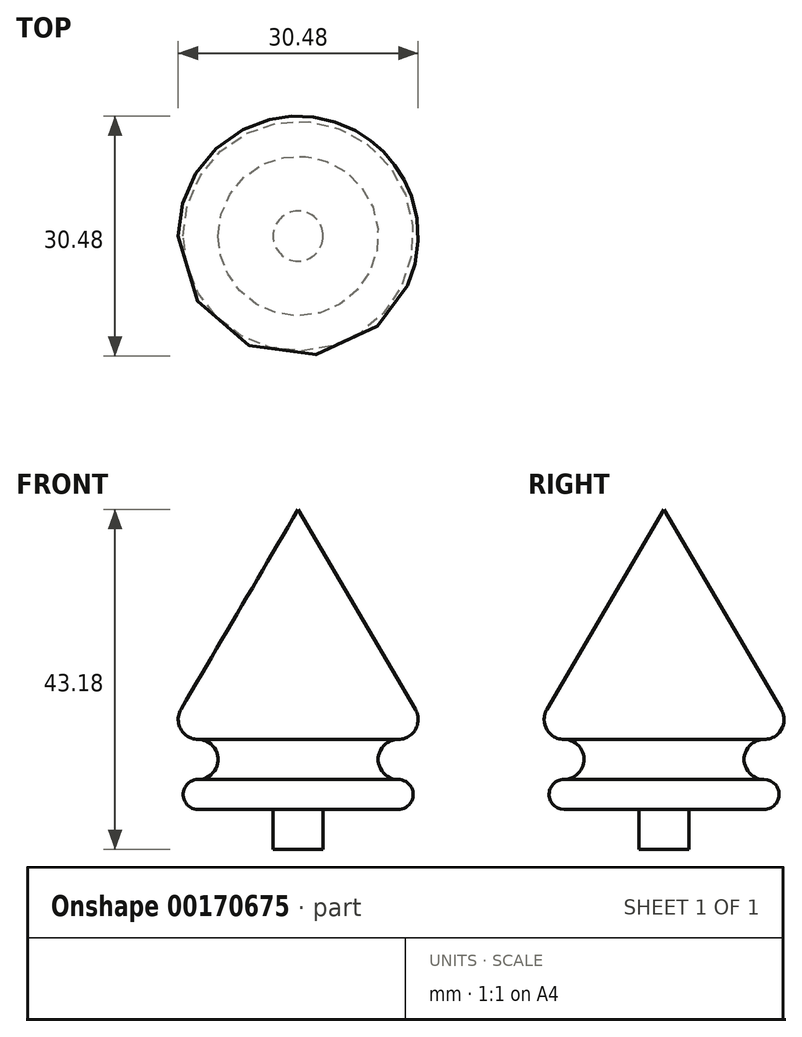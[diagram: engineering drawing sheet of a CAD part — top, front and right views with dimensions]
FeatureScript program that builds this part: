
annotation { "Feature Type Name" : "Feature", "Feature Type Description" : "" }
export const myFeature = defineFeature(function(context is Context, id is Id, definition is map)
    precondition{}
    {
        {
            var Q0;
            Q0=qCreatedBy(makeId("Front.planeOp"),FACE);
            var sketch = newSketch(context, id + "F0", { "sketchPlane" : qUnion([Q0])});
            skLineSegment(sketch, "E0", {"start": v(0, -5.08) * mm, "end": v(0, 38.1) * mm});
            skLineSegment(sketch, "E1", {"start": v(0, 38.1) * mm, "end": v(-14.9, 12.72) * mm});
            skLineSegment(sketch, "E2", {"start": v(0, -5.08) * mm, "end": v(-3.18, -5.08) * mm});
            skLineSegment(sketch, "E3", {"start": v(-3.18, -5.08) * mm, "end": v(-3.18, 0) * mm});
            skLineSegment(sketch, "E4", {"start": v(-3.18, 0) * mm, "end": v(-12.7, 0) * mm});
            skArc(sketch, "E5", {"start": v(-12.7, 3.81) * mm, "mid": v(-14.6, 1.9) * mm, "end": v(-12.7, 0) * mm});
            skArc(sketch, "E6", {"start": v(-12.7, 3.81) * mm, "mid": v(-10.16, 6.35) * mm, "end": v(-12.7, 8.9) * mm});
            skArc(sketch, "E7", {"start": v(-14.9, 12.72) * mm, "mid": v(-14.9, 10.17) * mm, "end": v(-12.7, 8.9) * mm});
            skSolve(sketch);
        }
        {
            var Q0;
            Q0=makeQuery(id+"F0.imprint","IMPRINT",FACE,{"disambiguationData":[TD([[makeQuery(id+"F0.imprint","IMPRINT",EDGE,{"derivedFrom":sQuery(id+"F0.wireOp",EDGE,"E0")}),1.0]])]});
            var Q1;
            Q1=sQuery(id+"F0.wireOp",EDGE,"E0");
            revolve(context, id + "F1", {"surfaceOperationType" : NewSurfaceOperationType.NEW, "entities" : qUnion([Q0]), "axis" : qUnion([Q1]), "revolveType" : RevolveType.FULL});
        }
    });
